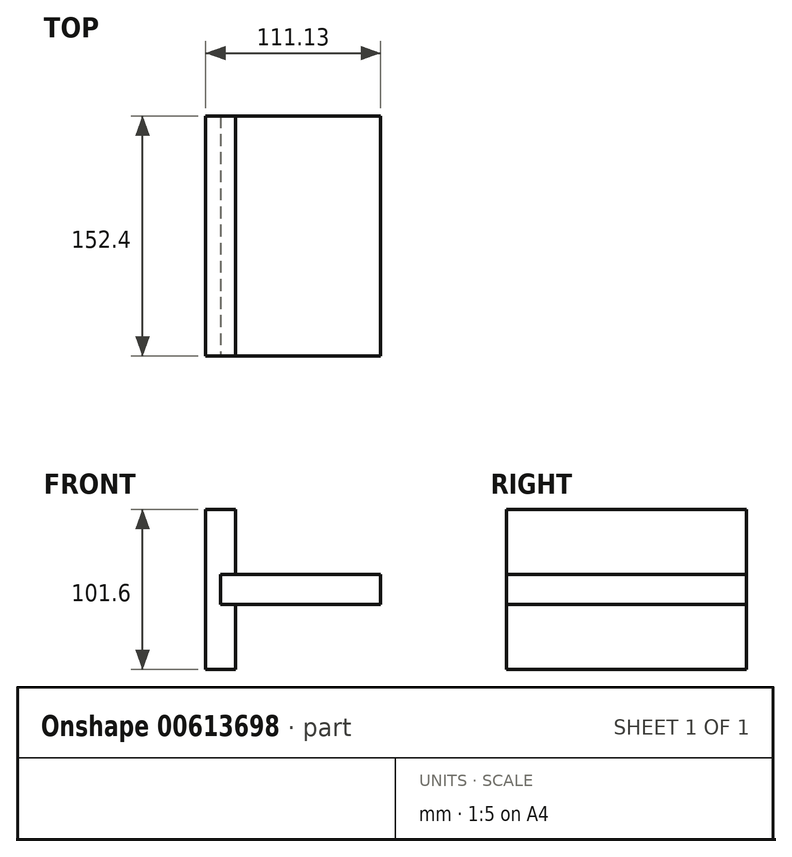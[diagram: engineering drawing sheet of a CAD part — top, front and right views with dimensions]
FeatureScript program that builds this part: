
annotation { "Feature Type Name" : "Feature", "Feature Type Description" : "" }
export const myFeature = defineFeature(function(context is Context, id is Id, definition is map)
    precondition{}
    {
        {
            var Q0;
            Q0=qCreatedBy(makeId("Top.planeOp"),FACE);
            var sketch = newSketch(context, id + "F0", { "sketchPlane" : qUnion([Q0])});
            skLineSegment(sketch, "E0.bottom", {"start": v(-9.52, 76.2) * mm, "end": v(9.53, 76.2) * mm});
            skLineSegment(sketch, "E0.top", {"start": v(-9.53, -76.2) * mm, "end": v(9.52, -76.2) * mm});
            skLineSegment(sketch, "E0.left", {"start": v(-9.52, 76.2) * mm, "end": v(-9.53, -76.2) * mm});
            skLineSegment(sketch, "E0.right", {"start": v(9.53, 76.2) * mm, "end": v(9.52, -76.2) * mm});
            skPoint(sketch, "E0.middle", {"position": v(0, 0) * mm});
            skSolve(sketch);
        }
        {
            var Q0;
            Q0 = qSketchRegion(id + "F0", true);
            extrude(context, id + "F1", {"entities" : qUnion([Q0]), "endBound" : BoundingType.SYMMETRIC, "depth" : 101.6 * mm, "offsetDistance" : 25.4 * mm});
        }
        {
            var Q0;
            Q0=makeQuery(id+"F1.opExtrude","SWEPT_FACE",FACE,{"disambiguationData":[OSD([sQuery(id+"F0.wireOp",EDGE,"E0.right")])]});
            var sketch = newSketch(context, id + "F2", { "sketchPlane" : qUnion([Q0])});
            skLineSegment(sketch, "E1.bottom", {"start": v(76.2, 9.53) * mm, "end": v(-76.2, 9.53) * mm});
            skLineSegment(sketch, "E1.top", {"start": v(76.2, -9.53) * mm, "end": v(-76.2, -9.53) * mm});
            skLineSegment(sketch, "E1.left", {"start": v(76.2, 9.53) * mm, "end": v(76.2, -9.53) * mm});
            skLineSegment(sketch, "E1.right", {"start": v(-76.2, 9.53) * mm, "end": v(-76.2, -9.53) * mm});
            skPoint(sketch, "E1.middle", {"position": v(0, 0) * mm});
            skSolve(sketch);
        }
        {
            var Q0;
            Q0 = qSketchRegion(id + "F2", true);
            extrude(context, id + "F3", {"entities" : qUnion([Q0]), "operationType" : NewBodyOperationType.REMOVE, "oppositeDirection" : true, "depth" : 9.52 * mm, "offsetDistance" : 25.4 * mm});
        }
        {
            var Q0;
            Q0=makeQuery(id+"F3.boolean.opBoolean","COPY",FACE,{"derivedFrom":makeQuery(id+"F3.opExtrude","CAP_FACE",FACE,{"disambiguationData":[OSD([sQuery(id+"F2.wireOp",EDGE,"E1.bottom"),sQuery(id+"F2.wireOp",EDGE,"E1.top"),sQuery(id+"F2.wireOp",EDGE,"E1.left"),sQuery(id+"F2.wireOp",EDGE,"E1.right")])],"isStart":false})});
            extrude(context, id + "F4", {"entities" : qUnion([Q0]), "depth" : 101.6 * mm, "offsetDistance" : 25.4 * mm});
        }
    });
